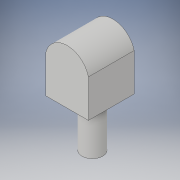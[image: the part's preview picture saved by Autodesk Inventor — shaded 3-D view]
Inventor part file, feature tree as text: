
AUTODESK INVENTOR PART (.ipt)
format: ipt  version: 2019 (Build 230136000, 136)  size: 100,864 bytes
history: native  units: mm
features: extrude x2, sketch x2
ambient origin geometry x8: Origin, YZ Plane, XZ Plane, XY Plane, X Axis, Y Axis, Z Axis, Center Point
bodies: Solid1 (feature_tree)
feature tree (4):
  extrude  "Extrusion1"  Depth=10.0mm TaperAngle=0.0deg
  extrude  "Extrusion2"  [1 undecoded]
  sketch  "Sketch1"  dims[d0=10.0mm d1=0.0mm d2=10.0mm d3=0.0mm]
  sketch  "Sketch2"
note: 1 required parameter value undecoded (feature->parameter linkage not recoverable at this tier; creation-order binding heuristic only, values carry confidence <= 0.55)
